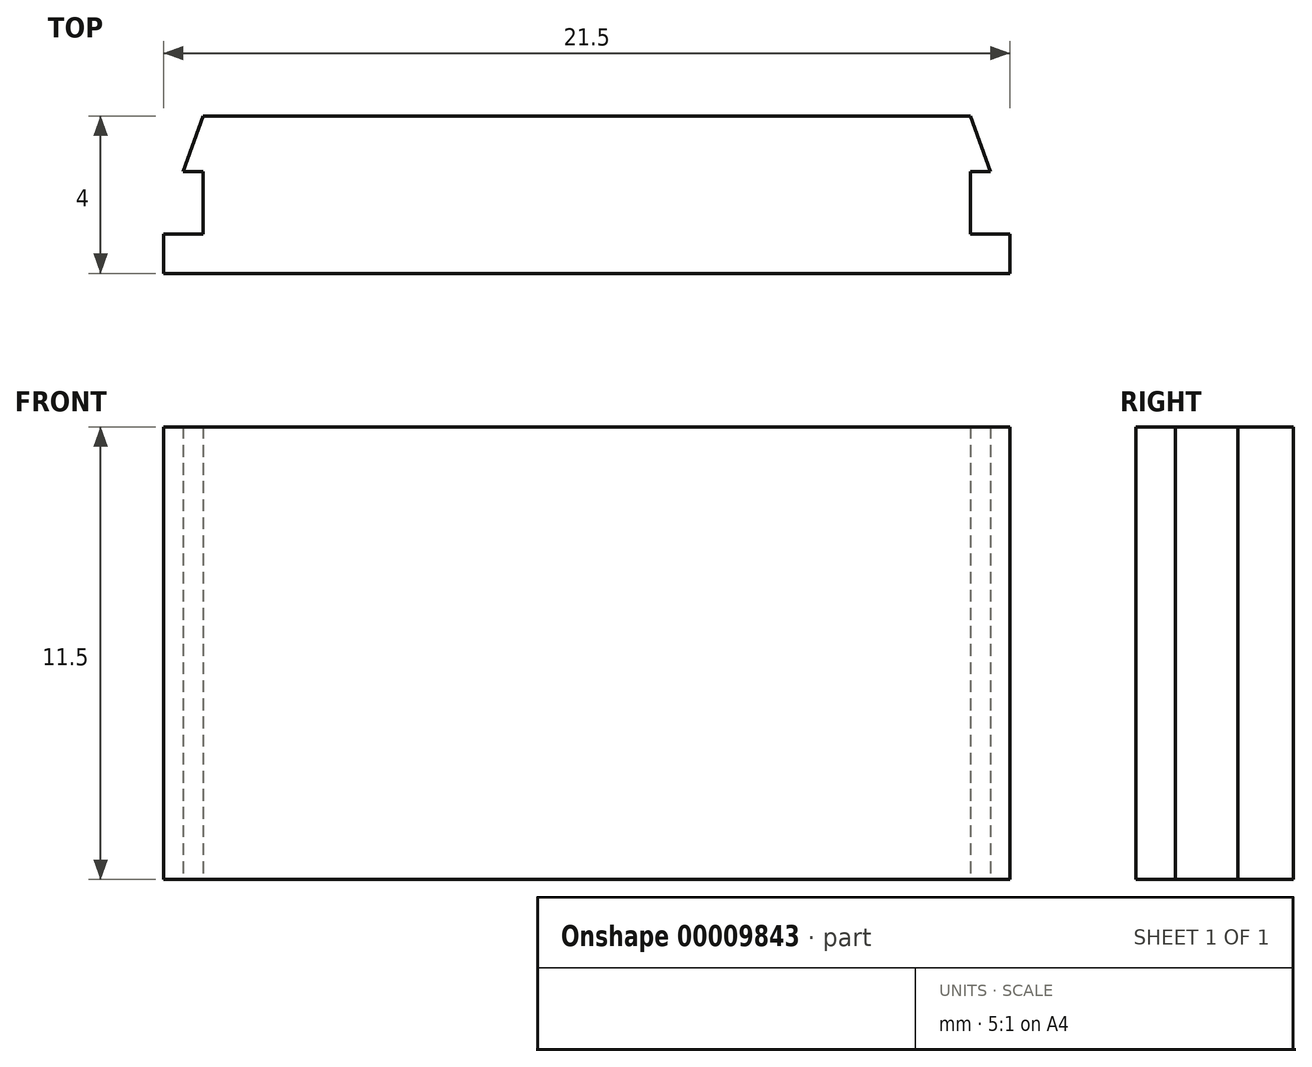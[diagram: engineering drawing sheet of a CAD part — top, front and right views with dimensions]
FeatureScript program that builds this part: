
annotation { "Feature Type Name" : "Feature", "Feature Type Description" : "" }
export const myFeature = defineFeature(function(context is Context, id is Id, definition is map)
    precondition{}
    {
        {
            var Q0;
            Q0=qCreatedBy(makeId("Top.planeOp"),FACE);
            var sketch = newSketch(context, id + "F0", { "sketchPlane" : qUnion([Q0])});
            skLineSegment(sketch, "E0.bottom", {"start": v(0, 0) * mm, "end": v(9.75, 0) * mm});
            skLineSegment(sketch, "E0.top", {"start": v(0, -4) * mm, "end": v(9.75, -4) * mm});
            skLineSegment(sketch, "E0.left", {"start": v(0, 0) * mm, "end": v(0, -4) * mm});
            skLineSegment(sketch, "E0.right", {"start": v(9.75, 0) * mm, "end": v(9.75, -4) * mm});
            skLineSegment(sketch, "E1", {"start": v(9.75, 0) * mm, "end": v(10.25, -1.41) * mm});
            skLineSegment(sketch, "E2.bottom", {"start": v(9.75, -4) * mm, "end": v(10.75, -4) * mm});
            skLineSegment(sketch, "E2.top", {"start": v(9.75, -3) * mm, "end": v(10.75, -3) * mm});
            skLineSegment(sketch, "E2.left", {"start": v(9.75, -4) * mm, "end": v(9.75, -3) * mm});
            skLineSegment(sketch, "E2.right", {"start": v(10.75, -4) * mm, "end": v(10.75, -3) * mm});
            skLineSegment(sketch, "E3", {"start": v(10.25, -1.41) * mm, "end": v(9.75, -1.41) * mm});
            skLineSegment(sketch, "E4.0.MirrorCS", {"start": v(0, 0) * mm, "end": v(-9.75, 0) * mm});
            skLineSegment(sketch, "E4.1.MirrorCS", {"start": v(0, -4) * mm, "end": v(-9.75, -4) * mm});
            skLineSegment(sketch, "E4.2.MirrorCS", {"start": v(-9.75, -4) * mm, "end": v(-9.75, -3) * mm});
            skLineSegment(sketch, "E4.3.MirrorCS", {"start": v(-10.25, -1.41) * mm, "end": v(-9.75, -1.41) * mm});
            skLineSegment(sketch, "E4.4.MirrorCS", {"start": v(-9.75, 0) * mm, "end": v(-9.75, -4) * mm});
            skLineSegment(sketch, "E4.5.MirrorCS", {"start": v(-9.75, 0) * mm, "end": v(-10.25, -1.41) * mm});
            skLineSegment(sketch, "E4.6.MirrorCS", {"start": v(-10.75, -4) * mm, "end": v(-10.75, -3) * mm});
            skLineSegment(sketch, "E4.7.MirrorCS", {"start": v(-9.75, -3) * mm, "end": v(-10.75, -3) * mm});
            skLineSegment(sketch, "E4.8.MirrorCS", {"start": v(-9.75, -4) * mm, "end": v(-10.75, -4) * mm});
            skSolve(sketch);
        }
        {
            var Q0;
            Q0 = qSketchRegion(id + "F0", true);
            extrude(context, id + "F1", {"entities" : qUnion([Q0]), "depth" : 11.5 * mm});
        }
    });
